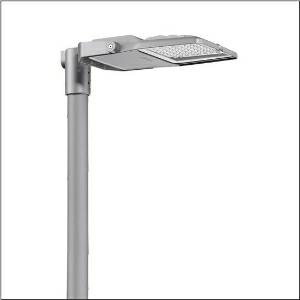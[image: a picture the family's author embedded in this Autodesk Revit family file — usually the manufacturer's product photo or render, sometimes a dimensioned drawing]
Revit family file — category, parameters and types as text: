
# Revit family: floodlight_fl_21_mini___pl61_5xa7775d2c3a_f3a4
name_source: partatom
category: Lighting Fixtures
units: mm (PartAtom-declared; Revit-internal decimal feet)

## family parameters
Cut with Voids When Loaded = No
Host = Face
Light Source = No
Part Type = Normal
Room Calculation Point = No
Round Connector Dimension = Use Diameter
Shared = No

## types (1)
- --- (1 x LED, 17510 lm, 142.9 W, 3000K)
    Apparent Load = 143 VA
    CIE Flux Codes = 33 65 98 100 100
    Color Rendering = 70
    Color Temperature = 3000K
    Default Elevation = 1800 mm
    Description = Floodlight FL 21 mini, floodlight, primary light control with lens, of PMMA, primary optical cover: protective disc, of toughened safety glass, transparent, light distribution: PL61, light emission: direct distribution, installation type: surface-mounted, LED, High Power LED, rated luminous flux: 17.510lm, luminous efficacy: 123lm/W, light colour: 730, colour temperature: 3000K, control gear: Smart Interface (Zhaga), control: flexible luminous flux parameterisation, time-dependent luminous flux control, constant luminous flux control, overheat protection, pre-setting: logarithmic dimming characteristic, with terminal, 6-pole, mains connection: 220..240V, AC, 50/60Hz, start of lifetime: 143W, end of service life: 151W, reduction: 63W, luminaire housing, of diecast aluminium, powder-coated, Siteco® metallic grey (DB 702S), corrosivity category C5 mid according to DIN EN ISO 12944, suitable for swimming pools, chlorine-resistant, sealing non-destructively replaceable, please order mast flange separately, mast bracket, of steel, galvanised, powder-coated, Siteco® metallic grey (DB 702S), Smart Interface above, protection rating (complete): IP66, insulation class (complete): insulation class II (safety insulation), certification: CE, ENEC, VDE, protection symbol: D, impact resistance: IK08, permissible operating ambient temperature: -40..+40°C, permissible operating ambient temperature for outdoor applications: -40..+50°C, standard: DIN EN 12944, LABS conformity tested according to VDMA 24364:2018-05, packaging unit: 1 piece

Light Distribution: PL61
    Height = 70 mm
    Lamp = 1 x LED
    Lamp Light Flux = 17510 lm
    Lamp Power = 142.9 W
    Lamp count = 1
    Length = 485 mm
    Luminous efficacy = 123 lm/W
    Manufacturer = Siteco
    ModVariant = No
    Model = 5XA7775D2C3A
    Number of Poles = 1
    OnlyDefault = Yes
    Power Factor = 1
    Product Name = Floodlight FL 21 mini | PL61
    Product group = floodlight | pylon annexe
    ProductGroupID = 6201
    Protection Class = Protection class II
    Protection Degree = IP 66
    RLX_Detail_Level = 1
    RLX_Emergency_Light_Flux = 0 lm
    RLX_Emergency_Type = 0
    RLX_Emergency_Type_DB = No
    RlxData = <blob elided: 101397 chars, md5=a5cef1c8>
    Socket = socket
    Standby Power = 0 W
    System Light Flux = 17510 lm
    System Power = 143 W
    Type Comments = factory setting: luminous flux: 100 % | dim-lin: 254 | 730 mA
    Type Image = l_1007125.jpg
    URL = http://relux.com
    VarID = @adj_193391
    Voltage = 0 V
    Weight = 0.00 kg
    Width = 337 mm

## geometry (parser evidence)
native form markers: Blend x4, Sweep x13
no freeform markers — native parametric forms only
